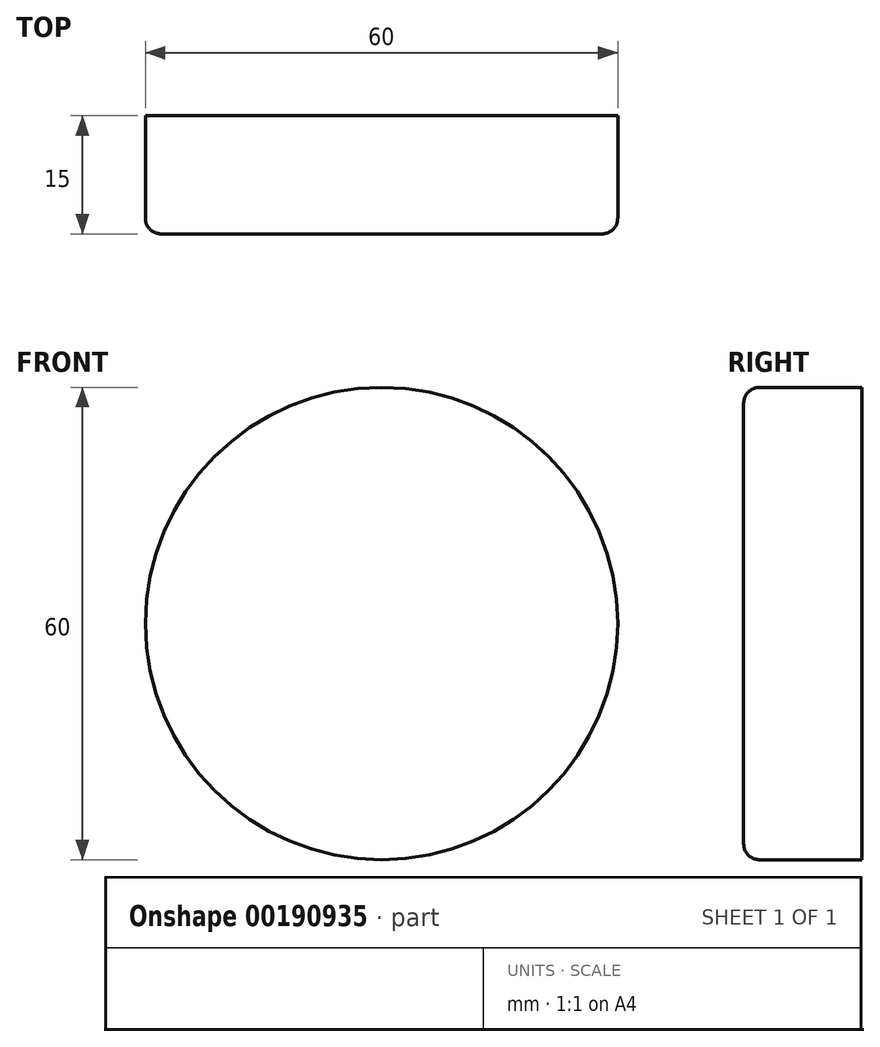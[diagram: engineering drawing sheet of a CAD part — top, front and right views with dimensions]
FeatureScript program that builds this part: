
annotation { "Feature Type Name" : "Feature", "Feature Type Description" : "" }
export const myFeature = defineFeature(function(context is Context, id is Id, definition is map)
    precondition{}
    {
        {
            var Q0;
            Q0=qCreatedBy(makeId("Front.planeOp"),FACE);
            var sketch = newSketch(context, id + "F0", { "sketchPlane" : qUnion([Q0])});
            skCircle(sketch, "E0", {"center": v(0, 0) * mm, "radius": 30 * mm});
            skSolve(sketch);
        }
        {
            var Q0;
            Q0 = qSketchRegion(id + "F0", true);
            extrude(context, id + "F1", {"entities" : qUnion([Q0]), "depth" : 15 * mm});
        }
        {
            var Q0;
            Q0=makeQuery(id+"F1.opExtrude","CAP_FACE",FACE,{"disambiguationData":[OSD([sQuery(id+"F0.wireOp",EDGE,"E0")])],"isStart":false});
            fillet(context, id + "F2", {"entities" : qUnion([Q0]), "radius" : 2 * mm, "tangentPropagation" : true, "allowEdgeOverflow" : false});
        }
    });
